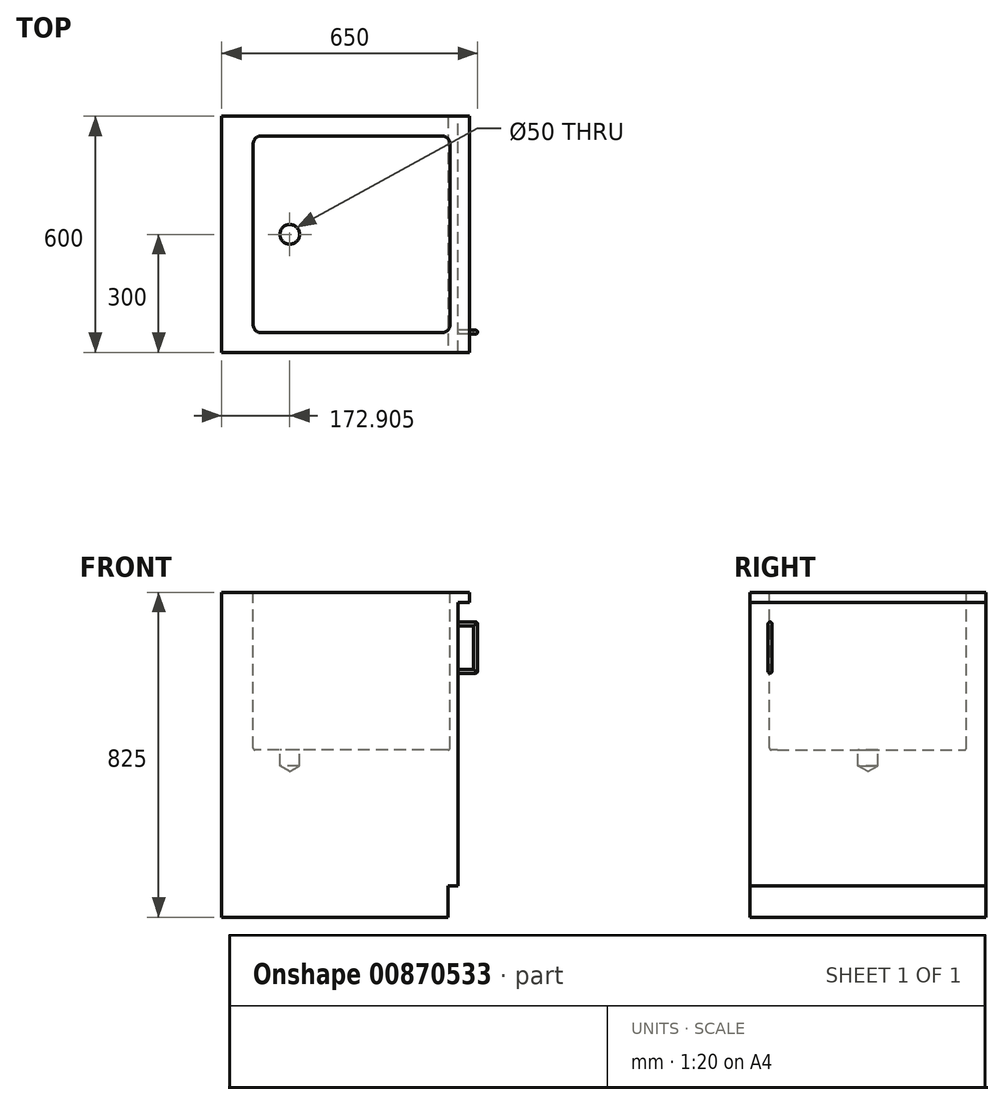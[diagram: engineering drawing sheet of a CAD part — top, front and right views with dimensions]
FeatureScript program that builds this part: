
annotation { "Feature Type Name" : "Feature", "Feature Type Description" : "" }
export const myFeature = defineFeature(function(context is Context, id is Id, definition is map)
    precondition{}
    {
        {
            var Q0;
            Q0=qCreatedBy(makeId("Top.planeOp"),FACE);
            var sketch = newSketch(context, id + "F0", { "sketchPlane" : qUnion([Q0])});
            skLineSegment(sketch, "E0.bottom", {"start": v(-300, 300) * mm, "end": v(300, 300) * mm});
            skLineSegment(sketch, "E0.top", {"start": v(-300, -300) * mm, "end": v(300, -300) * mm});
            skLineSegment(sketch, "E0.left", {"start": v(-300, 300) * mm, "end": v(-300, -300) * mm});
            skLineSegment(sketch, "E0.right", {"start": v(300, 300) * mm, "end": v(300, -300) * mm});
            skPoint(sketch, "E0.middle", {"position": v(0, 0) * mm});
            skSolve(sketch);
        }
        {
            var Q0;
            Q0=qSketchRegion(id+"F0",true);
            extrude(context, id + "F1", {"entities" : qUnion([Q0]), "depth" : 800 * mm, "offsetDistance" : 25 * mm});
        }
        {
            var Q0;
            Q0=makeQuery(id+"F1.opExtrude","SWEPT_FACE",FACE,{"disambiguationData":[OSD([sQuery(id+"F0.wireOp",EDGE,"E0.right")])]});
            var sketch = newSketch(context, id + "F2", { "sketchPlane" : qUnion([Q0])});
            skLineSegment(sketch, "E1.bottom", {"start": v(-300, 0) * mm, "end": v(300, 0) * mm});
            skLineSegment(sketch, "E1.top", {"start": v(-300, 80) * mm, "end": v(300, 80) * mm});
            skLineSegment(sketch, "E1.left", {"start": v(-300, 0) * mm, "end": v(-300, 80) * mm});
            skLineSegment(sketch, "E1.right", {"start": v(300, 0) * mm, "end": v(300, 80) * mm});
            skSolve(sketch);
        }
        {
            var Q0;
            Q0=qSketchRegion(id+"F2",true);
            extrude(context, id + "F3", {"entities" : qUnion([Q0]), "operationType" : NewBodyOperationType.REMOVE, "oppositeDirection" : true, "depth" : 25 * mm, "offsetDistance" : 25 * mm});
        }
        {
            var Q0;
            Q0=makeQuery(id+"F1.opExtrude","SWEPT_FACE",FACE,{"disambiguationData":[OSD([sQuery(id+"F0.wireOp",EDGE,"E0.right")])]});
            var sketch = newSketch(context, id + "F4", { "sketchPlane" : qUnion([Q0])});
            skLineSegment(sketch, "E2.bottom", {"start": v(-248.58, 750) * mm, "end": v(-248.58, 750) * mm});
            skLineSegment(sketch, "E2.top", {"start": v(-248.58, 620) * mm, "end": v(-248.58, 620) * mm});
            skLineSegment(sketch, "E2.left", {"start": v(-253.58, 745) * mm, "end": v(-253.58, 625) * mm});
            skLineSegment(sketch, "E2.right", {"start": v(-243.58, 745) * mm, "end": v(-243.58, 625) * mm});
            skPoint(sketch, "E3.visualSharp", {"position": v(-243.58, 750) * mm});
            skArc(sketch, "E3.filletArc", {"start": v(-243.58, 745) * mm, "mid": v(-245.04, 748.54) * mm, "end": v(-248.58, 750) * mm});
            skPoint(sketch, "E4.visualSharp", {"position": v(-243.58, 620) * mm});
            skArc(sketch, "E4.filletArc", {"start": v(-248.58, 620) * mm, "mid": v(-245.04, 621.46) * mm, "end": v(-243.58, 625) * mm});
            skPoint(sketch, "E5.visualSharp", {"position": v(-253.58, 620) * mm});
            skArc(sketch, "E5.filletArc", {"start": v(-253.58, 625) * mm, "mid": v(-252.12, 621.46) * mm, "end": v(-248.58, 620) * mm});
            skPoint(sketch, "E6.visualSharp", {"position": v(-253.58, 750) * mm});
            skArc(sketch, "E6.filletArc", {"start": v(-248.58, 750) * mm, "mid": v(-252.12, 748.54) * mm, "end": v(-253.58, 745) * mm});
            skSolve(sketch);
        }
        {
            var Q0;
            Q0=qSketchRegion(id+"F4",true);
            extrude(context, id + "F5", {"entities" : qUnion([Q0]), "operationType" : NewBodyOperationType.ADD, "depth" : 50 * mm, "offsetDistance" : 25 * mm});
        }
        {
            var Q0;
            Q0=makeQuery(id+"F5.opExtrude","CAP_FACE",FACE,{"disambiguationData":[OSD([sQuery(id+"F4.wireOp",EDGE,"E2.left"),sQuery(id+"F4.wireOp",EDGE,"E2.right"),sQuery(id+"F4.wireOp",EDGE,"E3.filletArc"),sQuery(id+"F4.wireOp",EDGE,"E4.filletArc"),sQuery(id+"F4.wireOp",EDGE,"E5.filletArc"),sQuery(id+"F4.wireOp",EDGE,"E6.filletArc")])],"isStart":false});
            fillet(context, id + "F6", {"entities" : qUnion([Q0]), "radius" : 5 * mm, "tangentPropagation" : true, "allowEdgeOverflow" : false});
        }
        {
            var Q0;
            Q0=makeQuery(id+"F5.opExtrude","SWEPT_FACE",FACE,{"disambiguationData":[OSD([sQuery(id+"F4.wireOp",EDGE,"E2.right")])]});
            var sketch = newSketch(context, id + "F7", { "sketchPlane" : qUnion([Q0])});
            skLineSegment(sketch, "E7.bottom", {"start": v(-340, 740) * mm, "end": v(-300, 740) * mm});
            skLineSegment(sketch, "E7.top", {"start": v(-340, 630) * mm, "end": v(-300, 630) * mm});
            skLineSegment(sketch, "E7.left", {"start": v(-340, 740) * mm, "end": v(-340, 630) * mm});
            skLineSegment(sketch, "E7.right", {"start": v(-300, 740) * mm, "end": v(-300, 630) * mm});
            skSolve(sketch);
        }
        {
            var Q0;
            Q0=makeQuery(id+"F7.imprint","IMPRINT",FACE,{"disambiguationData":[TD([[makeQuery(id+"F7.imprint","IMPRINT",EDGE,{"derivedFrom":sQuery(id+"F7.wireOp",EDGE,"E7.bottom")}),-1.0]])]});
            extrude(context, id + "F8", {"entities" : qUnion([Q0]), "operationType" : NewBodyOperationType.REMOVE, "oppositeDirection" : true, "depth" : 25 * mm, "offsetDistance" : 25 * mm});
        }
        {
            var Q0;
            Q0=makeQuery(id+"F8.boolean.opBoolean","COPY",EDGE,{"derivedFrom":makeQuery(id+"F8.opExtrude","CAP_EDGE",EDGE,{"disambiguationData":[OSD([sQuery(id+"F7.wireOp",EDGE,"E7.bottom")])],"isStart":true})});
            var Q1;
            Q1=makeQuery(id+"F8.boolean.opBoolean","COPY",EDGE,{"derivedFrom":makeQuery(id+"F8.opExtrude","CAP_EDGE",EDGE,{"disambiguationData":[OSD([sQuery(id+"F7.wireOp",EDGE,"E7.left")])],"isStart":true})});
            var Q2;
            Q2=makeQuery(id+"F8.boolean.opBoolean","COPY",EDGE,{"derivedFrom":makeQuery(id+"F8.opExtrude","CAP_EDGE",EDGE,{"disambiguationData":[OSD([sQuery(id+"F7.wireOp",EDGE,"E7.top")])],"isStart":true})});
            var Q3;
            Q3=makeQuery(id+"F8.boolean.opBoolean","INTERSECT",EDGE,{"derivedFrom":[makeQuery(id+"F5.opExtrude","SWEPT_FACE",FACE,{"disambiguationData":[OSD([sQuery(id+"F4.wireOp",EDGE,"E2.left")])]}),makeQuery(id+"F8.opExtrude","SWEPT_FACE",FACE,{"disambiguationData":[OSD([sQuery(id+"F7.wireOp",EDGE,"E7.bottom")])]})]});
            var Q4;
            Q4=makeQuery(id+"F8.boolean.opBoolean","INTERSECT",EDGE,{"derivedFrom":[makeQuery(id+"F5.opExtrude","SWEPT_FACE",FACE,{"disambiguationData":[OSD([sQuery(id+"F4.wireOp",EDGE,"E2.left")])]}),makeQuery(id+"F8.opExtrude","SWEPT_FACE",FACE,{"disambiguationData":[OSD([sQuery(id+"F7.wireOp",EDGE,"E7.left")])]})]});
            var Q5;
            Q5=makeQuery(id+"F8.boolean.opBoolean","INTERSECT",EDGE,{"derivedFrom":[makeQuery(id+"F5.opExtrude","SWEPT_FACE",FACE,{"disambiguationData":[OSD([sQuery(id+"F4.wireOp",EDGE,"E2.left")])]}),makeQuery(id+"F8.opExtrude","SWEPT_FACE",FACE,{"disambiguationData":[OSD([sQuery(id+"F7.wireOp",EDGE,"E7.top")])]})]});
            fillet(context, id + "F9", {"entities" : qUnion([Q0, Q1, Q2, Q3, Q4, Q5]), "radius" : 5 * mm, "tangentPropagation" : true, "allowEdgeOverflow" : false});
        }
        {
            var Q0;
            Q0=makeQuery(id+"F1.opExtrude","CAP_FACE",FACE,{"disambiguationData":[OSD([sQuery(id+"F0.wireOp",EDGE,"E0.bottom"),sQuery(id+"F0.wireOp",EDGE,"E0.top"),sQuery(id+"F0.wireOp",EDGE,"E0.left"),sQuery(id+"F0.wireOp",EDGE,"E0.right")])],"isStart":false});
            var sketch = newSketch(context, id + "F10", { "sketchPlane" : qUnion([Q0])});
            skLineSegment(sketch, "E8.bottom", {"start": v(-300, -300) * mm, "end": v(330, -300) * mm});
            skLineSegment(sketch, "E8.top", {"start": v(-300, 300) * mm, "end": v(330, 300) * mm});
            skLineSegment(sketch, "E8.left", {"start": v(-300, -300) * mm, "end": v(-300, 300) * mm});
            skLineSegment(sketch, "E8.right", {"start": v(330, -300) * mm, "end": v(330, 300) * mm});
            skSolve(sketch);
        }
        {
            var Q0;
            Q0=qSketchRegion(id+"F10",true);
            extrude(context, id + "F11", {"entities" : qUnion([Q0]), "operationType" : NewBodyOperationType.ADD, "depth" : 25 * mm, "offsetDistance" : 25 * mm});
        }
        {
            var Q0;
            Q0=makeQuery(id+"F11.opExtrude","CAP_FACE",FACE,{"disambiguationData":[OSD([sQuery(id+"F10.wireOp",EDGE,"E8.bottom"),sQuery(id+"F10.wireOp",EDGE,"E8.top"),sQuery(id+"F10.wireOp",EDGE,"E8.left"),sQuery(id+"F10.wireOp",EDGE,"E8.right")])],"isStart":false});
            var sketch = newSketch(context, id + "F12", { "sketchPlane" : qUnion([Q0])});
            skLineSegment(sketch, "E9.bottom", {"start": v(260, -250) * mm, "end": v(-200, -250) * mm});
            skLineSegment(sketch, "E9.top", {"start": v(260, 250) * mm, "end": v(-200, 250) * mm});
            skLineSegment(sketch, "E9.left", {"start": v(280, -230) * mm, "end": v(280, 230) * mm});
            skLineSegment(sketch, "E9.right", {"start": v(-220, -230) * mm, "end": v(-220, 230) * mm});
            skPoint(sketch, "E10.visualSharp", {"position": v(-220, -250) * mm});
            skArc(sketch, "E10.filletArc", {"start": v(-220, -230) * mm, "mid": v(-214.14, -244.14) * mm, "end": v(-200, -250) * mm});
            skPoint(sketch, "E11.visualSharp", {"position": v(-220, 250) * mm});
            skArc(sketch, "E11.filletArc", {"start": v(-200, 250) * mm, "mid": v(-214.14, 244.14) * mm, "end": v(-220, 230) * mm});
            skPoint(sketch, "E12.visualSharp", {"position": v(280, 250) * mm});
            skArc(sketch, "E12.filletArc", {"start": v(280, 230) * mm, "mid": v(274.14, 244.14) * mm, "end": v(260, 250) * mm});
            skPoint(sketch, "E13.visualSharp", {"position": v(280, -250) * mm});
            skArc(sketch, "E13.filletArc", {"start": v(260, -250) * mm, "mid": v(274.14, -244.14) * mm, "end": v(280, -230) * mm});
            skSolve(sketch);
        }
        {
            var Q0;
            Q0 = qSketchRegion(id + "F12", true);
            extrude(context, id + "F13", {"entities" : qUnion([Q0]), "operationType" : NewBodyOperationType.REMOVE, "oppositeDirection" : true, "depth" : 400 * mm, "offsetDistance" : 25 * mm});
        }
        {
            var Q0;
            Q0=makeQuery(id+"F13.boolean.opBoolean","COPY",EDGE,{"derivedFrom":makeQuery(id+"F13.opExtrude","CAP_EDGE",EDGE,{"disambiguationData":[OSD([sQuery(id+"F12.wireOp",EDGE,"E9.top")])],"isStart":false})});
            var Q1;
            Q1=makeQuery(id+"F13.boolean.opBoolean","COPY",EDGE,{"derivedFrom":makeQuery(id+"F13.opExtrude","CAP_EDGE",EDGE,{"disambiguationData":[OSD([sQuery(id+"F12.wireOp",EDGE,"E11.filletArc")])],"isStart":false})});
            var Q2;
            Q2=makeQuery(id+"F13.boolean.opBoolean","COPY",EDGE,{"derivedFrom":makeQuery(id+"F13.opExtrude","CAP_EDGE",EDGE,{"disambiguationData":[OSD([sQuery(id+"F12.wireOp",EDGE,"E9.right")])],"isStart":false})});
            var Q3;
            Q3=makeQuery(id+"F13.boolean.opBoolean","COPY",FACE,{"derivedFrom":makeQuery(id+"F13.opExtrude","CAP_FACE",FACE,{"disambiguationData":[OSD([sQuery(id+"F12.wireOp",EDGE,"E9.bottom"),sQuery(id+"F12.wireOp",EDGE,"E9.top"),sQuery(id+"F12.wireOp",EDGE,"E9.left"),sQuery(id+"F12.wireOp",EDGE,"E9.right"),sQuery(id+"F12.wireOp",EDGE,"E10.filletArc"),sQuery(id+"F12.wireOp",EDGE,"E11.filletArc"),sQuery(id+"F12.wireOp",EDGE,"E12.filletArc"),sQuery(id+"F12.wireOp",EDGE,"E13.filletArc")])],"isStart":false})});
            fillet(context, id + "F14", {"entities" : qUnion([Q0, Q1, Q2, Q3]), "radius" : 5 * mm, "tangentPropagation" : true, "allowEdgeOverflow" : false});
        }
        {
            var Q0;
            Q0=makeQuery(id+"F13.boolean.opBoolean","COPY",FACE,{"derivedFrom":makeQuery(id+"F13.opExtrude","CAP_FACE",FACE,{"disambiguationData":[OSD([sQuery(id+"F12.wireOp",EDGE,"E9.bottom"),sQuery(id+"F12.wireOp",EDGE,"E9.top"),sQuery(id+"F12.wireOp",EDGE,"E9.left"),sQuery(id+"F12.wireOp",EDGE,"E9.right"),sQuery(id+"F12.wireOp",EDGE,"E10.filletArc"),sQuery(id+"F12.wireOp",EDGE,"E11.filletArc"),sQuery(id+"F12.wireOp",EDGE,"E12.filletArc"),sQuery(id+"F12.wireOp",EDGE,"E13.filletArc")])],"isStart":false})});
            var sketch = newSketch(context, id + "F15", { "sketchPlane" : qUnion([Q0])});
            skPoint(sketch, "E14", {"position": v(-127.1, 0) * mm});
            skSolve(sketch);
        }
        {
            var Q0;
            Q0=sQuery(id+"F15.wireOp",VERTEX,"E14");
            var Q1;
            Q1=makeQuery(id+"F1.opExtrude","SWEPT_BODY",BODY,{"disambiguationData":[OSD([sQuery(id+"F0.wireOp",EDGE,"E0.bottom"),sQuery(id+"F0.wireOp",EDGE,"E0.top"),sQuery(id+"F0.wireOp",EDGE,"E0.left"),sQuery(id+"F0.wireOp",EDGE,"E0.right")])]});
            hole(context, id + "F16", {"style" : HoleStyle.SIMPLE, "endStyle" : HoleEndStyle.BLIND, "holeDiameter" : 50 * mm, "majorDiameter" : 5 * mm, "holeDepth" : 40 * mm, "isTappedThrough" : true, "tappedDepth" : 12 * mm, "tapClearance" : 3, "locations" : qUnion([Q0]), "scope" : qUnion([Q1])});
        }
    });
